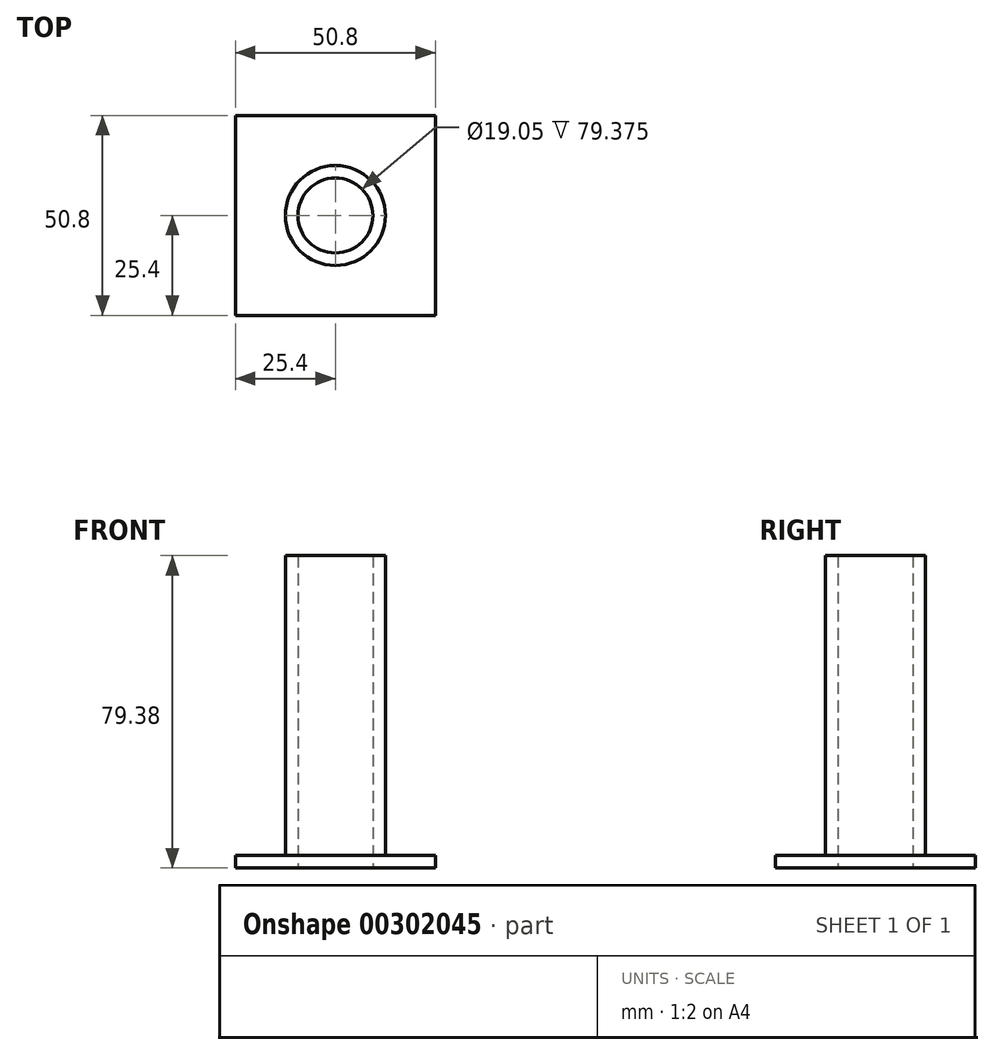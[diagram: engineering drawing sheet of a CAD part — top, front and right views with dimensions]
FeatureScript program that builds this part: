
annotation { "Feature Type Name" : "Feature", "Feature Type Description" : "" }
export const myFeature = defineFeature(function(context is Context, id is Id, definition is map)
    precondition{}
    {
        {
            var Q0;
            Q0=qCreatedBy(makeId("Top.planeOp"),FACE);
            var sketch = newSketch(context, id + "F0", { "sketchPlane" : qUnion([Q0])});
            skCircle(sketch, "E0", {"center": v(0, 0) * mm, "radius": 12.7 * mm});
            skCircle(sketch, "E1", {"center": v(0, 0) * mm, "radius": 9.53 * mm});
            skSolve(sketch);
        }
        {
            var Q0;
            Q0 = qSketchRegion(id + "F0", true);
            extrude(context, id + "F1", {"entities" : qUnion([Q0]), "depth" : 76.2 * mm});
        }
        {
            var Q0;
            Q0=qCreatedBy(makeId("Top.planeOp"),FACE);
            var sketch = newSketch(context, id + "F2", { "sketchPlane" : qUnion([Q0])});
            skCircle(sketch, "E2", {"center": v(0, 0) * mm, "radius": 9.53 * mm});
            skLineSegment(sketch, "E3.bottom", {"start": v(25.4, -25.4) * mm, "end": v(-25.4, -25.4) * mm});
            skLineSegment(sketch, "E3.top", {"start": v(25.4, 25.4) * mm, "end": v(-25.4, 25.4) * mm});
            skLineSegment(sketch, "E3.left", {"start": v(25.4, -25.4) * mm, "end": v(25.4, 25.4) * mm});
            skLineSegment(sketch, "E3.right", {"start": v(-25.4, -25.4) * mm, "end": v(-25.4, 25.4) * mm});
            skSolve(sketch);
        }
        {
            var Q0;
            Q0=makeQuery(id+"F2.imprint","IMPRINT",FACE,{"disambiguationData":[TD([[makeQuery(id+"F2.imprint","IMPRINT",EDGE,{"derivedFrom":sQuery(id+"F2.wireOp",EDGE,"E2")}),-1.0]])]});
            extrude(context, id + "F3", {"entities" : qUnion([Q0]), "operationType" : NewBodyOperationType.ADD, "oppositeDirection" : true, "depth" : 3.17 * mm});
        }
    });
